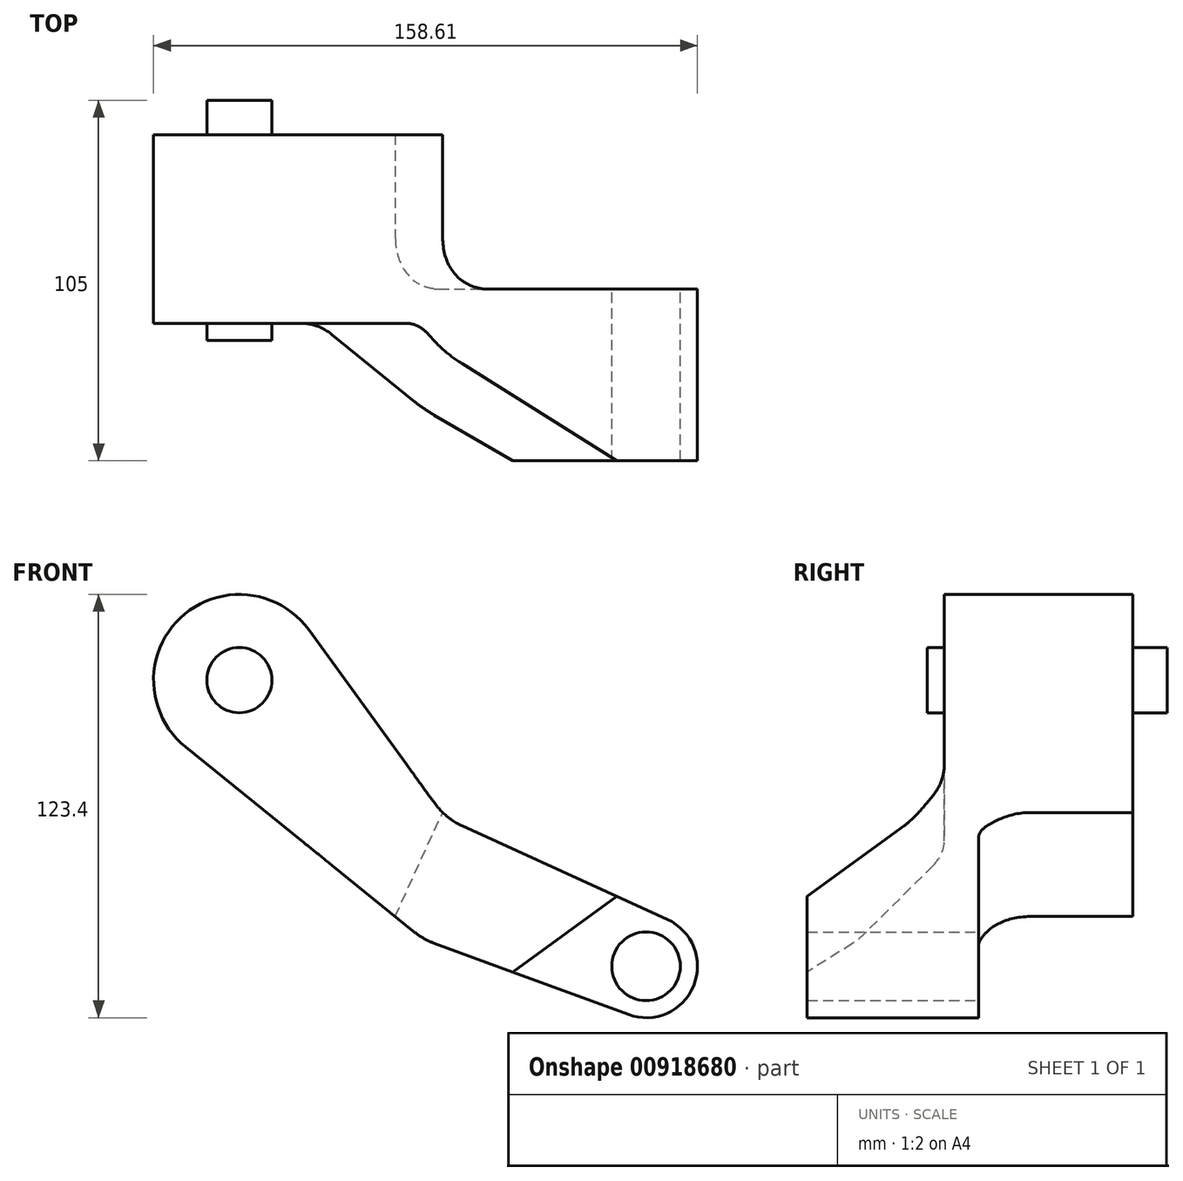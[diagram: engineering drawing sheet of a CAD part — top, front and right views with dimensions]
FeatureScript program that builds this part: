
annotation { "Feature Type Name" : "Feature", "Feature Type Description" : "" }
export const myFeature = defineFeature(function(context is Context, id is Id, definition is map)
    precondition{}
    {
        {
            var Q0;
            Q0=qCreatedBy(makeId("Front.planeOp"),FACE);
            var sketch = newSketch(context, id + "F0", { "sketchPlane" : qUnion([Q0])});
            skCircle(sketch, "E0", {"center": v(-19.7, 88.12) * mm, "radius": 9.5 * mm});
            skCircle(sketch, "E1", {"center": v(98.9, 4.72) * mm, "radius": 10 * mm});
            skArc(sketch, "E2", {"start": v(0.52, 102.82) * mm, "mid": v(-36.93, 106.25) * mm, "end": v(-35.42, 68.68) * mm});
            skLineSegment(sketch, "E3", {"start": v(0.52, 102.82) * mm, "end": v(40.47, 47.84) * mm});
            skLineSegment(sketch, "E4", {"start": v(40.47, 47.84) * mm, "end": v(105.13, 18.37) * mm});
            skArc(sketch, "E5", {"start": v(93.74, -9.37) * mm, "mid": v(112.78, -0.98) * mm, "end": v(105.13, 18.37) * mm});
            skLineSegment(sketch, "E6", {"start": v(-35.42, 68.68) * mm, "end": v(34.04, 12.53) * mm});
            skLineSegment(sketch, "E7", {"start": v(34.04, 12.53) * mm, "end": v(93.74, -9.37) * mm});
            skSolve(sketch);
        }
        {
            var Q0;
            Q0 = qSketchRegion(id + "F0", true);
            extrude(context, id + "F1", {"entities" : qUnion([Q0]), "depth" : 95 * mm, "offsetDistance" : 25 * mm});
        }
        {
            var Q0;
            Q0=makeQuery(id+"F1.opExtrude","SWEPT_FACE",FACE,{"disambiguationData":[OSD([sQuery(id+"F0.wireOp",EDGE,"E3")])]});
            var sketch = newSketch(context, id + "F2", { "sketchPlane" : qUnion([Q0])});
            skLineSegment(sketch, "E8.bottom", {"start": v(-55, 107.92) * mm, "end": v(-95, 107.92) * mm});
            skLineSegment(sketch, "E8.left", {"start": v(-55, 107.92) * mm, "end": v(-55, 28.27) * mm});
            skLineSegment(sketch, "E8.right", {"start": v(-95, 107.92) * mm, "end": v(-95, -12.08) * mm});
            skPoint(sketch, "E9.visualSharp", {"position": v(-55, 10.07) * mm});
            skLineSegment(sketch, "E10", {"start": v(-55, 28.27) * mm, "end": v(-95, -32.87) * mm});
            skLineSegment(sketch, "E11", {"start": v(-95, -32.87) * mm, "end": v(-95, -12.08) * mm});
            skSolve(sketch);
        }
        {
            var Q0;
            Q0 = qSketchRegion(id + "F2", true);
            extrude(context, id + "F3", {"entities" : qUnion([Q0]), "operationType" : NewBodyOperationType.REMOVE, "endBound" : BoundingType.THROUGH_ALL, "oppositeDirection" : true, "depth" : 25 * mm, "offsetDistance" : 25 * mm, "hasSecondDirection" : true, "secondDirectionBound" : BoundingType.THROUGH_ALL, "secondDirectionOppositeDirection" : false, "secondDirectionDepth" : 25 * mm});
        }
        {
            var Q0;
            Q0=makeQuery(id+"F1.opExtrude","SWEPT_FACE",FACE,{"disambiguationData":[OSD([sQuery(id+"F0.wireOp",EDGE,"E4")])]});
            var sketch = newSketch(context, id + "F4", { "sketchPlane" : qUnion([Q0])});
            skLineSegment(sketch, "E12.bottom", {"start": v(15.47, 0) * mm, "end": v(126.87, 0) * mm});
            skLineSegment(sketch, "E12.top", {"start": v(15.47, -45) * mm, "end": v(126.87, -45) * mm});
            skLineSegment(sketch, "E12.left", {"start": v(15.47, 0) * mm, "end": v(15.47, -45) * mm});
            skLineSegment(sketch, "E12.right", {"start": v(126.87, 0) * mm, "end": v(126.87, -45) * mm});
            skSolve(sketch);
        }
        {
            var Q0;
            Q0 = qSketchRegion(id + "F4", true);
            extrude(context, id + "F5", {"entities" : qUnion([Q0]), "operationType" : NewBodyOperationType.REMOVE, "endBound" : BoundingType.THROUGH_ALL, "oppositeDirection" : true, "depth" : 25 * mm, "offsetDistance" : 25 * mm, "hasSecondDirection" : true, "secondDirectionOppositeDirection" : false, "secondDirectionDepth" : 25 * mm});
        }
        {
            var Q0;
            Q0=makeQuery(id+"F5.boolean.opBoolean","COPY",EDGE,{"derivedFrom":makeQuery(id+"F5.opExtrude","SWEPT_EDGE",EDGE,{"disambiguationData":[OSD([sQuery(id+"F4.wireOp",EDGE,"E12.top"),sQuery(id+"F4.wireOp",EDGE,"E12.left")])]})});
            var Q1;
            Q1=makeQuery(id+"F5.boolean.opBoolean","COPY",EDGE,{"derivedFrom":makeQuery(id+"F5.opExtrude","SWEPT_EDGE",EDGE,{"disambiguationData":[OSD([sQuery(id+"F0.wireOp",EDGE,"E4"),sQuery(id+"F4.wireOp",EDGE,"E12.bottom"),sQuery(id+"F4.wireOp",EDGE,"E12.left")])]})});
            fillet(context, id + "F6", {"entities" : qUnion([Q0, Q1]), "radius" : 15 * mm, "tangentPropagation" : true, "allowEdgeOverflow" : false});
        }
        {
            var Q0;
            {var subQ0=sQuery(id+"F0.wireOp",EDGE,"E3");var subQ1=sQuery(id+"F0.wireOp",EDGE,"E4");Q0=makeQuery(id+"F5.boolean.opBoolean","SPLIT",EDGE,{"disambiguationData":[topologyDisambiguationEdgeConnected([makeQuery(id+"F1.opExtrude","SWEPT_FACE",FACE,{"disambiguationData":[OSD([subQ1])]})])],"derivedFrom":makeQuery(id+"F3.boolean.opBoolean","SPLIT",EDGE,{"derivedFrom":makeQuery(id+"F1.opExtrude","SWEPT_EDGE",EDGE,{"disambiguationData":[OSD([subQ0,subQ1])]})})});}
            var Q1;
            Q1=makeQuery(id+"F1.opExtrude","SWEPT_EDGE",EDGE,{"disambiguationData":[OSD([sQuery(id+"F0.wireOp",EDGE,"E6"),sQuery(id+"F0.wireOp",EDGE,"E7")])]});
            fillet(context, id + "F7", {"entities" : qUnion([Q0, Q1]), "radius" : 20 * mm, "tangentPropagation" : true, "allowEdgeOverflow" : false});
        }
        {
            var Q0;
            Q0=makeQuery(id+"F3.boolean.opBoolean","COPY",FACE,{"derivedFrom":makeQuery(id+"F3.opExtrude","SWEPT_FACE",FACE,{"disambiguationData":[OSD([sQuery(id+"F2.wireOp",EDGE,"E8.left")])]})});
            var sketch = newSketch(context, id + "F8", { "sketchPlane" : qUnion([Q0])});
            skCircle(sketch, "E13", {"center": v(-19.7, 88.12) * mm, "radius": 9.5 * mm});
            skSolve(sketch);
        }
        {
            var Q0;
            Q0 = qSketchRegion(id + "F8", true);
            extrude(context, id + "F9", {"entities" : qUnion([Q0]), "operationType" : NewBodyOperationType.ADD, "depth" : 5 * mm, "offsetDistance" : 25 * mm, "hasSecondDirection" : true, "secondDirectionOppositeDirection" : true, "secondDirectionDepth" : 65 * mm});
        }
        {
            var Q0;
            Q0=makeQuery(id+"F3.boolean.opBoolean","COPY",EDGE,{"derivedFrom":makeQuery(id+"F3.opExtrude","SWEPT_EDGE",EDGE,{"disambiguationData":[OSD([sQuery(id+"F2.wireOp",EDGE,"E8.left"),sQuery(id+"F2.wireOp",EDGE,"E10")])]})});
            var Q1;
            Q1=makeQuery(id+"F3.boolean.opBoolean","COPY",EDGE,{"derivedFrom":makeQuery(id+"F3.opExtrude","SWEPT_EDGE",EDGE,{"disambiguationData":[OSD([sQuery(id+"F2.wireOp",EDGE,"E10"),sQuery(id+"F2.wireOp",EDGE,"E11")])]})});
            fillet(context, id + "F10", {"entities" : qUnion([Q0, Q1]), "radius" : 20 * mm, "tangentPropagation" : true, "allowEdgeOverflow" : false});
        }
    });
